# Revit family: Shower-Shower_Column_Kit-KOHLER-ACCLIV-K-33087T_1
name_source: partatom
category: Plumbing Fixtures
revit_build: Autodesk Revit 2017 (Build: 20160225_1515(x64)
units: mm (PartAtom-declared; Revit-internal decimal feet)

## family parameters
Cut with Voids When Loaded = No
Host = Face
OmniClass Number = 23.31.17.00
OmniClass Title = Showers
Part Type = Normal
Room Calculation Point = No
Round Connector Dimension = Use Diameter
Shared = No

## types (3) — shared parameters
ADA Compliant = No
Assembly Code = D2010700
CW Connection = Yes
Cold Water Inlet = Cold Water Inlet
Date Modified = 11/26/2021
Default Elevation = 36"
Description = 3 WAY SHOWER COLUMN DIRECT
Drain Included = No
Flow Rate = 3 GPM
HW Connection = Yes
Handle Clearance = 3 3/8"
Height = 48 7/16"
Hot Water Inlet = Hot Water Inlet
Length = 23 11/16"
Manufacturer = KOHLER Co.
Master Format 2014 = 22 42 23
Master Format 2014 Name = Residential Showers
Material = Premium Metal Construction
Pressure = 80.00 psi
Product Name = ACCLIV
Spout Reach = 4 1/2"
URL = http://www.kohler.com.cn
Vent Connection = No
Waste Connection = No
Waste Water Outlet = Waste Water Outlet
WaterSense Certified = No
Width = 5 15/16"

## per-type parameters (varying)
| type | Finish | Model | Nozzle & Face Plate Finish | Type |
| CP-Polished Chrome | Kohler-Metal-CP-Polished_Chrome | K-33087T-4-CP | Kohler-Plastic-0-White | 1 |
| AF-Flange Gold | Kohler-Metal-AF-Flange_Gold | K-33087T-4-AF | Kohler-Plastic-0-White | 2 |
| BN-Roman Silver | Kohler-Metal-BN-Roman_Silver | K-33087T-4-BN | Kohler-Plastic-95-Ice_Grey | 3 |

## geometry (parser evidence)
native form markers: Sweep x6
no freeform markers — native parametric forms only
